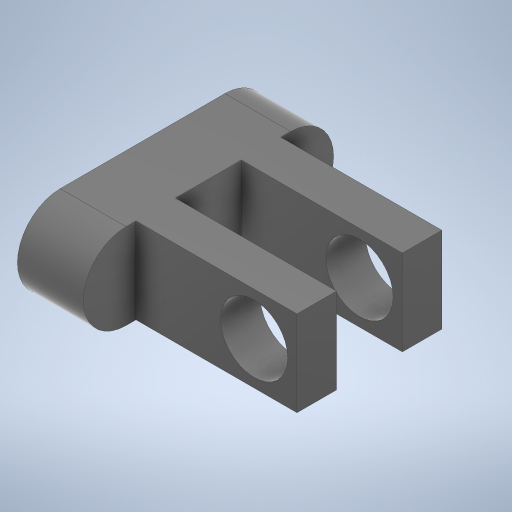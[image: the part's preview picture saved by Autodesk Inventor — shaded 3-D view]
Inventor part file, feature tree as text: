
AUTODESK INVENTOR PART (.ipt)
format: ipt  version: 2023 (Build 270158000, 158)  size: 303,104 bytes
history: native  units: mm
features: extrude x5, plane x4, sketch x4
ambient origin geometry x8: Origin, YZ Plane, XZ Plane, XY Plane, X Axis, Y Axis, Z Axis, Center Point
bodies: Volumenkörper1 (feature_tree)
feature tree (13):
  extrude  "Extrusion1"  Depth=13.0mm
  extrude  "Extrusion2"  Depth=12.5mm
  plane  "Arbeitsebene1"
  extrude  "Extrusion3"  Depth=10.0mm
  plane  "Arbeitsebene2"
  extrude  "Extrusion4"  Depth=6.0mm TaperAngle=0.0deg
  extrude  "Extrusion5"  Depth=13.0mm
  plane  "Arbeitsebene3"
  plane  "Arbeitsebene4"
  sketch  "Skizze1"  dims[d0=13.0mm d1=13.0mm]
  sketch  "Skizze2"  dims[d2=12.5mm d3=12.5mm]
  sketch  "Skizze4"  dims[d6=10.0mm d7=0.0mm d8=10.1mm]
  sketch  "Skizze6"  dims[d9=10.1mm d10=6.0mm d11=0.0mm d12=5.0mm d13=6.0mm d14=0.0mm d15=-5.0mm d17=6.0mm d18=0.0mm d20=10.2mm d21=0.0mm d22=0.0mm d24=0.0mm d25=0.0mm d26=24.445639mm d27=13.0mm]
